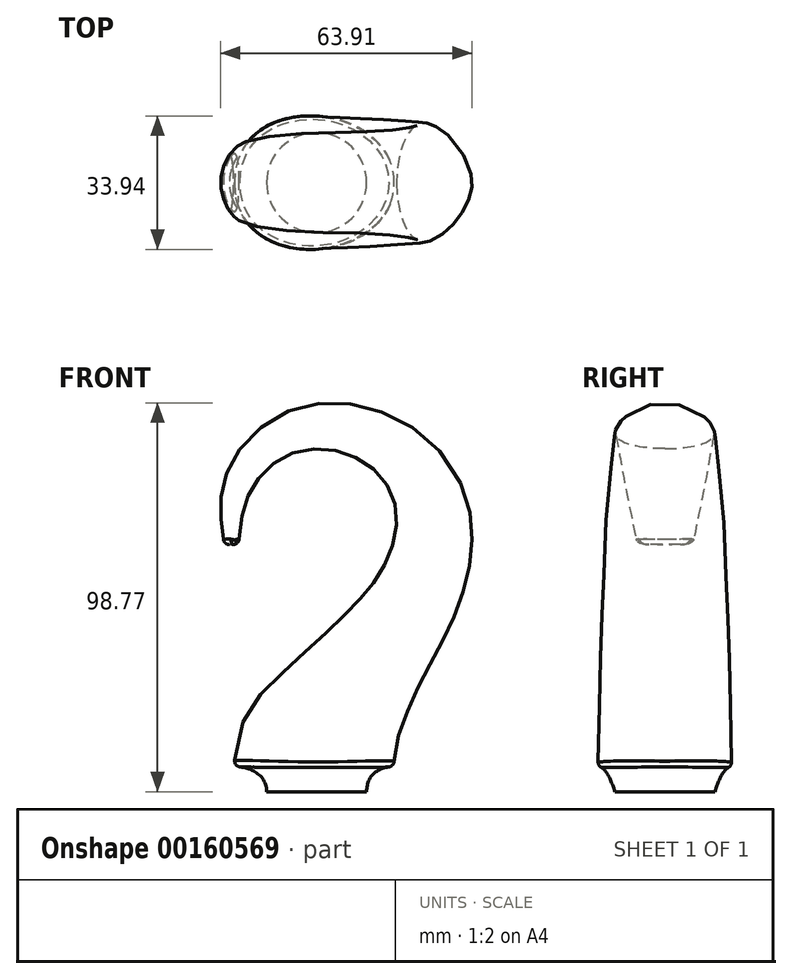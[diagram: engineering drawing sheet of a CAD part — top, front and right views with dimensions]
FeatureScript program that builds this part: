
annotation { "Feature Type Name" : "Feature", "Feature Type Description" : "" }
export const myFeature = defineFeature(function(context is Context, id is Id, definition is map)
    precondition{}
    {
        {
            var Q0;
            Q0=qCreatedBy(makeId("Front.planeOp"),FACE);
            var sketch = newSketch(context, id + "F0", { "sketchPlane" : qUnion([Q0])});
            skFitSpline(sketch, "E0", {"points": [v(-20.88, 0) * mm, v(-8.18, 24.36) * mm, v(6.88, 38.33) * mm, v(16.43, 49.82) * mm, v(20.3, 63.6) * mm, v(14, 76.05) * mm, v(-2.92, 80.53) * mm, v(-15.61, 72.06) * mm, v(-19.79, 56.46) * mm], "startDerivative": vector(0, 244.58) * mm, "endDerivative": vector(-10.5, -156.23) * mm});
            skFitSpline(sketch, "E1", {"points": [v(19.66, 0) * mm, v(22.72, 13.2) * mm, v(28.88, 26.12) * mm, v(36.61, 42.56) * mm, v(38.67, 65.9) * mm, v(23.2, 86.93) * mm, v(-5.21, 91.04) * mm, v(-22.74, 74.84) * mm, v(-23.47, 56.34) * mm], "startDerivative": vector(0, 140.08) * mm, "endDerivative": vector(27.53, -159.04) * mm});
            skLineSegment(sketch, "E2", {"start": v(-20.88, 0) * mm, "end": v(-20.88, 29.57) * mm});
            skLineSegment(sketch, "E3", {"start": v(19.66, 0) * mm, "end": v(19.66, 23.38) * mm});
            skLineSegment(sketch, "E4", {"start": v(-20.88, 0) * mm, "end": v(19.66, 0) * mm});
            skLineSegment(sketch, "E5", {"start": v(-8.18, 24.36) * mm, "end": v(22.72, 13.2) * mm});
            skLineSegment(sketch, "E6", {"start": v(6.88, 38.33) * mm, "end": v(28.88, 26.12) * mm});
            skLineSegment(sketch, "E7", {"start": v(16.43, 49.82) * mm, "end": v(36.61, 42.56) * mm});
            skLineSegment(sketch, "E8", {"start": v(-23.47, 56.34) * mm, "end": v(-19.79, 56.46) * mm});
            skLineSegment(sketch, "E9", {"start": v(20.3, 63.6) * mm, "end": v(38.67, 65.9) * mm});
            skLineSegment(sketch, "E10", {"start": v(14, 76.05) * mm, "end": v(23.2, 86.93) * mm});
            skLineSegment(sketch, "E11", {"start": v(-2.92, 80.53) * mm, "end": v(-5.21, 91.04) * mm});
            skLineSegment(sketch, "E12", {"start": v(-15.61, 72.06) * mm, "end": v(-22.74, 74.84) * mm});
            skLineSegment(sketch, "E13.0", {"start": v(-20.5, -6.35) * mm, "end": v(21.88, -6.35) * mm});
            skLineSegment(sketch, "E14", {"start": v(0, 0) * mm, "end": v(0, -6.35) * mm});
            skFitSpline(sketch, "E15", {"points": [v(-20.88, 0) * mm, v(-12.7, -6.35) * mm], "startDerivative": vector(11.63, 0) * mm, "endDerivative": vector(0, -13.38) * mm});
            skLineSegment(sketch, "E16", {"start": v(-12.7, -6.35) * mm, "end": v(-12.7, 2.57) * mm});
            skFitSpline(sketch, "E17", {"points": [v(12.7, -6.35) * mm, v(19.66, 0) * mm], "startDerivative": vector(0, 13.6) * mm, "endDerivative": vector(10.69, 0) * mm});
            skLineSegment(sketch, "E18", {"start": v(12.7, -6.35) * mm, "end": v(12.7, 2.71) * mm});
            skLineSegment(sketch, "E19", {"start": v(-12.7, -6.35) * mm, "end": v(-12.7, -39.69) * mm});
            skLineSegment(sketch, "E20", {"start": v(12.7, -6.35) * mm, "end": v(12.7, -39.69) * mm});
            skLineSegment(sketch, "E21", {"start": v(-12.7, -39.69) * mm, "end": v(12.7, -39.69) * mm});
            skLineSegment(sketch, "E22", {"start": v(-12.7, -39.69) * mm, "end": v(-12.7, -42.74) * mm});
            skLineSegment(sketch, "E23", {"start": v(-12.7, -42.74) * mm, "end": v(-9.97, -41.04) * mm});
            skLineSegment(sketch, "E24", {"start": v(-9.97, -41.04) * mm, "end": v(-12.7, -39.69) * mm});
            skLineSegment(sketch, "E25", {"start": v(12.7, -36.94) * mm, "end": v(10.62, -40.4) * mm});
            skLineSegment(sketch, "E26", {"start": v(12.7, -39.69) * mm, "end": v(12.7, -41.21) * mm});
            skPoint(sketch, "E26.endSnap0", {"position": v(-12.7, -41.21) * mm});
            skLineSegment(sketch, "E27", {"start": v(10.62, -40.4) * mm, "end": v(12.7, -40.4) * mm});
            skSolve(sketch);
        }
        {
            var Q0;
            Q0 = qSketchRegion(id + "F0", true);
            var Q1;
            Q1=sQuery(id+"F0.wireOp",EDGE,"E4");
            extrude(context, id + "F1", {"entities" : qUnion([Q0]), "bodyType" : ToolBodyType.SURFACE, "surfaceEntities" : qUnion([Q1]), "endBound" : BoundingType.SYMMETRIC, "depth" : 38.1 * mm});
        }
        {
            var Q0;
            Q0 = qSketchRegion(id + "F0", true);
            var Q1;
            Q1=sQuery(id+"F0.wireOp",EDGE,"E5");
            extrude(context, id + "F2", {"entities" : qUnion([Q0]), "bodyType" : ToolBodyType.SURFACE, "surfaceEntities" : qUnion([Q1]), "endBound" : BoundingType.SYMMETRIC, "depth" : 38.1 * mm});
        }
        {
            var Q0;
            Q0=sQuery(id+"F0.wireOp",EDGE,"E6");
            extrude(context, id + "F3", {"bodyType" : ToolBodyType.SURFACE, "surfaceEntities" : qUnion([Q0]), "endBound" : BoundingType.SYMMETRIC, "depth" : 38.1 * mm});
        }
        {
            var Q0;
            {var subQ0=sQuery(id+"F0.wireOp",EDGE,"E6");Q0=makeQuery(id+"F0.imprint","IMPRINT",FACE,{"disambiguationData":[TD([[makeQuery(id+"F0.imprint","IMPRINT",EDGE,{"derivedFrom":subQ0}),1.0]])]});}
            var Q1;
            Q1=sQuery(id+"F0.wireOp",EDGE,"E7");
            extrude(context, id + "F4", {"entities" : qUnion([Q0]), "bodyType" : ToolBodyType.SURFACE, "surfaceEntities" : qUnion([Q1]), "endBound" : BoundingType.SYMMETRIC, "depth" : 38.1 * mm});
        }
        {
            var Q0;
            Q0=sQuery(id+"F0.wireOp",EDGE,"E9");
            extrude(context, id + "F5", {"bodyType" : ToolBodyType.SURFACE, "surfaceEntities" : qUnion([Q0]), "endBound" : BoundingType.SYMMETRIC, "depth" : 38.1 * mm});
        }
        {
            var Q0;
            Q0=sQuery(id+"F0.wireOp",EDGE,"E10");
            extrude(context, id + "F6", {"bodyType" : ToolBodyType.SURFACE, "surfaceEntities" : qUnion([Q0]), "endBound" : BoundingType.SYMMETRIC, "depth" : 31.75 * mm});
        }
        {
            var Q0;
            Q0=sQuery(id+"F0.wireOp",EDGE,"E11");
            extrude(context, id + "F7", {"bodyType" : ToolBodyType.SURFACE, "surfaceEntities" : qUnion([Q0]), "endBound" : BoundingType.SYMMETRIC, "depth" : 31.75 * mm});
        }
        {
            var Q0;
            Q0=sQuery(id+"F0.wireOp",EDGE,"E12");
            extrude(context, id + "F8", {"bodyType" : ToolBodyType.SURFACE, "surfaceEntities" : qUnion([Q0]), "endBound" : BoundingType.SYMMETRIC, "depth" : 28.57 * mm});
        }
        {
            var Q0;
            Q0 = qSketchRegion(id + "F0", true);
            var Q1;
            Q1=sQuery(id+"F0.wireOp",EDGE,"E8");
            extrude(context, id + "F9", {"entities" : qUnion([Q0]), "bodyType" : ToolBodyType.SURFACE, "surfaceEntities" : qUnion([Q1]), "endBound" : BoundingType.SYMMETRIC, "depth" : 25.4 * mm});
        }
        {
            var Q0;
            Q0=makeQuery(id+"F1.opExtrude","SWEPT_FACE",FACE,{"disambiguationData":[OSD([sQuery(id+"F0.wireOp",EDGE,"E4")])]});
            var sketch = newSketch(context, id + "F10", { "sketchPlane" : qUnion([Q0])});
            skFitSpline(sketch, "E28", {"points": [v(-20.88, 0) * mm, v(1.09, -16.87) * mm, v(19.66, 0) * mm], "startDerivative": vector(0, -77.44) * mm, "endDerivative": vector(0, 61.25) * mm});
            skFitSpline(sketch, "E29.MirrorCS", {"points": [v(-20.88, 0) * mm, v(1.09, 16.87) * mm, v(19.66, 0) * mm], "startDerivative": vector(0, 77.44) * mm, "endDerivative": vector(0, -61.25) * mm});
            skSolve(sketch);
        }
        {
            var Q0;
            Q0=makeQuery(id+"F2.opExtrude","SWEPT_FACE",FACE,{"disambiguationData":[OSD([sQuery(id+"F0.wireOp",EDGE,"E5")])]});
            var sketch = newSketch(context, id + "F11", { "sketchPlane" : qUnion([Q0])});
            skFitSpline(sketch, "E30", {"points": [v(-15.97, 0) * mm, v(-3.43, -16.52) * mm, v(16.88, 0) * mm], "startDerivative": vector(0, -47.06) * mm, "endDerivative": vector(0, 47.26) * mm});
            skFitSpline(sketch, "E31.MirrorCS", {"points": [v(-15.97, 0) * mm, v(-3.43, 16.52) * mm, v(16.88, 0) * mm], "startDerivative": vector(0, 47.06) * mm, "endDerivative": vector(0, -47.26) * mm});
            skSolve(sketch);
        }
        {
            var Q0;
            Q0=makeQuery(id+"F3.opExtrude","SWEPT_FACE",FACE,{"disambiguationData":[OSD([sQuery(id+"F0.wireOp",EDGE,"E6")])]});
            var sketch = newSketch(context, id + "F12", { "sketchPlane" : qUnion([Q0])});
            skFitSpline(sketch, "E32", {"points": [v(-12.59, 0) * mm, v(-4.6, -16.15) * mm, v(12.57, 0) * mm], "startDerivative": vector(0, -57.35) * mm, "endDerivative": vector(0, 43.44) * mm});
            skFitSpline(sketch, "E33.MirrorCS", {"points": [v(-12.59, 0) * mm, v(-4.6, 16.15) * mm, v(12.57, 0) * mm], "startDerivative": vector(0, 57.35) * mm, "endDerivative": vector(0, -43.44) * mm});
            skSolve(sketch);
        }
        {
            var Q0;
            Q0=makeQuery(id+"F4.opExtrude","SWEPT_FACE",FACE,{"disambiguationData":[OSD([sQuery(id+"F0.wireOp",EDGE,"E7")])]});
            var sketch = newSketch(context, id + "F13", { "sketchPlane" : qUnion([Q0])});
            skFitSpline(sketch, "E34", {"points": [v(-1.38, 0) * mm, v(6.22, -15.51) * mm, v(20.07, 0) * mm], "startDerivative": vector(0, -37.32) * mm, "endDerivative": vector(0, 31.05) * mm});
            skFitSpline(sketch, "E35.MirrorCS", {"points": [v(-1.38, 0) * mm, v(6.22, 15.51) * mm, v(20.07, 0) * mm], "startDerivative": vector(0, 37.32) * mm, "endDerivative": vector(0, -31.05) * mm});
            skSolve(sketch);
        }
        {
            var Q0;
            Q0=makeQuery(id+"F5.opExtrude","SWEPT_FACE",FACE,{"disambiguationData":[OSD([sQuery(id+"F0.wireOp",EDGE,"E9")])]});
            var sketch = newSketch(context, id + "F14", { "sketchPlane" : qUnion([Q0])});
            skFitSpline(sketch, "E36", {"points": [v(28.03, 0) * mm, v(34.37, -14.78) * mm, v(46.54, 0) * mm], "startDerivative": vector(0, -41.23) * mm, "endDerivative": vector(0, 41.24) * mm});
            skFitSpline(sketch, "E37.MirrorCS", {"points": [v(28.03, 0) * mm, v(34.37, 14.78) * mm, v(46.54, 0) * mm], "startDerivative": vector(0, 41.23) * mm, "endDerivative": vector(0, -41.24) * mm});
            skSolve(sketch);
        }
        {
            var Q0;
            Q0=makeQuery(id+"F6.opExtrude","SWEPT_FACE",FACE,{"disambiguationData":[OSD([sQuery(id+"F0.wireOp",EDGE,"E10")])]});
            var sketch = newSketch(context, id + "F15", { "sketchPlane" : qUnion([Q0])});
            skFitSpline(sketch, "E38", {"points": [v(0, 67.14) * mm, v(13.2, 71.95) * mm, v(0, 81.38) * mm], "startDerivative": vector(47.39, 0) * mm, "endDerivative": vector(-38.47, 0) * mm});
            skFitSpline(sketch, "E39.MirrorCS", {"points": [v(0, 67.14) * mm, v(-13.2, 71.95) * mm, v(0, 81.38) * mm], "startDerivative": vector(-47.39, 0) * mm, "endDerivative": vector(38.47, 0) * mm});
            skSolve(sketch);
        }
        {
            var Q0;
            Q0=makeQuery(id+"F7.opExtrude","SWEPT_FACE",FACE,{"disambiguationData":[OSD([sQuery(id+"F0.wireOp",EDGE,"E11")])]});
            var sketch = newSketch(context, id + "F16", { "sketchPlane" : qUnion([Q0])});
            skFitSpline(sketch, "E40", {"points": [v(0, 79.3) * mm, v(-12.36, 82.69) * mm, v(0, 90.06) * mm], "startDerivative": vector(-27.64, 0) * mm, "endDerivative": vector(39.98, 0) * mm});
            skFitSpline(sketch, "E41.MirrorCS", {"points": [v(0, 79.3) * mm, v(12.36, 82.69) * mm, v(0, 90.06) * mm], "startDerivative": vector(27.64, 0) * mm, "endDerivative": vector(-39.98, 0) * mm});
            skSolve(sketch);
        }
        {
            var Q0;
            Q0=makeQuery(id+"F8.opExtrude","SWEPT_FACE",FACE,{"disambiguationData":[OSD([sQuery(id+"F0.wireOp",EDGE,"E12")])]});
            var sketch = newSketch(context, id + "F17", { "sketchPlane" : qUnion([Q0])});
            skFitSpline(sketch, "E42", {"points": [v(-40.71, 0) * mm, v(-42.92, -10.35) * mm, v(-48.37, 0) * mm], "startDerivative": vector(0, -20.7) * mm, "endDerivative": vector(0, 25.7) * mm});
            skFitSpline(sketch, "E43.MirrorCS", {"points": [v(-40.71, 0) * mm, v(-42.92, 10.35) * mm, v(-48.37, 0) * mm], "startDerivative": vector(0, 20.7) * mm, "endDerivative": vector(0, -25.7) * mm});
            skSolve(sketch);
        }
        {
            var Q0;
            Q0=makeQuery(id+"F9.opExtrude","SWEPT_FACE",FACE,{"disambiguationData":[OSD([sQuery(id+"F0.wireOp",EDGE,"E8")])]});
            var sketch = newSketch(context, id + "F18", { "sketchPlane" : qUnion([Q0])});
            skFitSpline(sketch, "E44", {"points": [v(-17.94, 0) * mm, v(-18.9, 7.05) * mm, v(-21.62, 0) * mm], "startDerivative": vector(0, 12.16) * mm, "endDerivative": vector(0, -22.35) * mm});
            skFitSpline(sketch, "E45.MirrorCS", {"points": [v(-17.94, 0) * mm, v(-18.9, -7.05) * mm, v(-21.62, 0) * mm], "startDerivative": vector(0, -12.16) * mm, "endDerivative": vector(0, 22.35) * mm});
            skSolve(sketch);
        }
        {
            var Q0;
            Q0 = qSketchRegion(id + "F0", true);
            var Q1;
            Q1=sQuery(id+"F0.wireOp",EDGE,"E13.0");
            extrude(context, id + "F19", {"entities" : qUnion([Q0]), "bodyType" : ToolBodyType.SURFACE, "surfaceEntities" : qUnion([Q1]), "endBound" : BoundingType.SYMMETRIC, "depth" : 25.4 * mm});
        }
        {
            var Q0;
            Q0=makeQuery(id+"F19.opExtrude","SWEPT_FACE",FACE,{"disambiguationData":[OSD([sQuery(id+"F0.wireOp",EDGE,"E13.0")])]});
            var sketch = newSketch(context, id + "F20", { "sketchPlane" : qUnion([Q0])});
            skCircle(sketch, "E46", {"center": v(0, 0) * mm, "radius": 12.7 * mm});
            skSolve(sketch);
        }
        {
            var Q0;
            Q0=makeQuery(id+"F10.imprint","IMPRINT",FACE,{"disambiguationData":[TD([[makeQuery(id+"F10.imprint","IMPRINT",EDGE,{"derivedFrom":sQuery(id+"F10.wireOp",EDGE,"E28")}),1.0]])]});
            var Q1;
            {var subQ0=sQuery(id+"F20.wireOp",EDGE,"E46");var subQ1=sQuery(id+"F0.wireOp",EDGE,"E13.0");var subQ2=makeQuery(id+"F20.imprint","INTERSECT",VERTEX,{"derivedFrom":[makeQuery(id+"F19.opExtrude","CAP_EDGE",EDGE,{"disambiguationData":[OSD([subQ1])],"isStart":true}),subQ0]});Q1=makeQuery(id+"F20.imprint","IMPRINT",FACE,{"disambiguationData":[TD([[makeQuery(id+"F20.imprint","IMPRINT",EDGE,{"disambiguationData":[TD([[subQ2,1.0]])],"derivedFrom":subQ0}),1.0]])]});}
            var Q2;
            Q2=sQuery(id+"F0.wireOp",EDGE,"E15");
            var Q3;
            Q3=sQuery(id+"F0.wireOp",EDGE,"E17");
            loft(context, id + "F21", {"addGuides" : true, "sheetProfilesArray" : [{ "sheetProfileEntities" : qUnion([Q0]) }, { "sheetProfileEntities" : qUnion([Q1]) }], "guidesArray" : [{ "guideEntities" : qUnion([Q2]), "guideDerivativeType" : LoftGuideDerivativeType.DEFAULT, "guideDerivativeMagnitude" : 1 }, { "guideEntities" : qUnion([Q3]), "guideDerivativeType" : LoftGuideDerivativeType.DEFAULT, "guideDerivativeMagnitude" : 1 }]});
        }
        {
            var Q0;
            Q0=makeQuery(id+"F10.imprint","IMPRINT",FACE,{"disambiguationData":[TD([[makeQuery(id+"F10.imprint","IMPRINT",EDGE,{"derivedFrom":sQuery(id+"F10.wireOp",EDGE,"E28")}),1.0]])]});
            var Q1;
            Q1=makeQuery(id+"F11.imprint","IMPRINT",FACE,{"disambiguationData":[TD([[makeQuery(id+"F11.imprint","IMPRINT",EDGE,{"derivedFrom":sQuery(id+"F11.wireOp",EDGE,"E30")}),1.0]])]});
            var Q2;
            Q2=makeQuery(id+"F12.imprint","IMPRINT",FACE,{"disambiguationData":[TD([[makeQuery(id+"F12.imprint","IMPRINT",EDGE,{"derivedFrom":sQuery(id+"F12.wireOp",EDGE,"E32")}),1.0]])]});
            var Q3;
            Q3=makeQuery(id+"F13.imprint","IMPRINT",FACE,{"disambiguationData":[TD([[makeQuery(id+"F13.imprint","IMPRINT",EDGE,{"derivedFrom":sQuery(id+"F13.wireOp",EDGE,"E34")}),1.0]])]});
            var Q4;
            {var subQ1=sQuery(id+"F14.wireOp",EDGE,"E36");var subQ3=makeQuery(id+"F5.opExtrude","SWEPT_EDGE",EDGE,{"disambiguationData":[OSD([sQuery(id+"F0.wireOp",VERTEX,"E9.start")])]});var subQ4=makeQuery(id+"F14.imprint","INTERSECT",VERTEX,{"derivedFrom":[subQ3,subQ1]});Q4=makeQuery(id+"F14.imprint","IMPRINT",FACE,{"disambiguationData":[TD([[makeQuery(id+"F14.imprint","IMPRINT",EDGE,{"disambiguationData":[TD([[subQ4,-1.0]])],"derivedFrom":subQ1}),1.0]])]});}
            var Q5;
            Q5=makeQuery(id+"F15.imprint","IMPRINT",FACE,{"disambiguationData":[TD([[makeQuery(id+"F15.imprint","IMPRINT",EDGE,{"derivedFrom":sQuery(id+"F15.wireOp",EDGE,"E38")}),1.0]])]});
            var Q6;
            {var subQ1=sQuery(id+"F16.wireOp",EDGE,"E40");var subQ3=makeQuery(id+"F7.opExtrude","SWEPT_EDGE",EDGE,{"disambiguationData":[OSD([sQuery(id+"F0.wireOp",VERTEX,"E11.start")])]});var subQ4=makeQuery(id+"F16.imprint","INTERSECT",VERTEX,{"derivedFrom":[subQ3,subQ1]});Q6=makeQuery(id+"F16.imprint","IMPRINT",FACE,{"disambiguationData":[TD([[makeQuery(id+"F16.imprint","IMPRINT",EDGE,{"disambiguationData":[TD([[subQ4,-1.0]])],"derivedFrom":subQ1}),-1.0]])]});}
            var Q7;
            Q7=makeQuery(id+"F17.imprint","IMPRINT",FACE,{"disambiguationData":[TD([[makeQuery(id+"F17.imprint","IMPRINT",EDGE,{"derivedFrom":sQuery(id+"F17.wireOp",EDGE,"E42")}),-1.0]])]});
            var Q8;
            {var subQ1=sQuery(id+"F18.wireOp",EDGE,"E44");var subQ3=makeQuery(id+"F9.opExtrude","SWEPT_EDGE",EDGE,{"disambiguationData":[OSD([sQuery(id+"F0.wireOp",VERTEX,"E8.end")])]});var subQ4=makeQuery(id+"F18.imprint","INTERSECT",VERTEX,{"derivedFrom":[subQ3,subQ1]});Q8=makeQuery(id+"F18.imprint","IMPRINT",FACE,{"disambiguationData":[TD([[makeQuery(id+"F18.imprint","IMPRINT",EDGE,{"disambiguationData":[TD([[subQ4,-1.0]])],"derivedFrom":subQ1}),1.0]])]});}
            var Q9;
            Q9=sQuery(id+"F0.wireOp",EDGE,"E0");
            var Q10;
            Q10=sQuery(id+"F0.wireOp",EDGE,"E1");
            loft(context, id + "F22", {"addGuides" : true, "sheetProfilesArray" : [{ "sheetProfileEntities" : qUnion([Q0]) }, { "sheetProfileEntities" : qUnion([Q1]) }, { "sheetProfileEntities" : qUnion([Q2]) }, { "sheetProfileEntities" : qUnion([Q3]) }, { "sheetProfileEntities" : qUnion([Q4]) }, { "sheetProfileEntities" : qUnion([Q5]) }, { "sheetProfileEntities" : qUnion([Q6]) }, { "sheetProfileEntities" : qUnion([Q7]) }, { "sheetProfileEntities" : qUnion([Q8]) }], "guidesArray" : [{ "guideEntities" : qUnion([Q9]), "guideDerivativeType" : LoftGuideDerivativeType.DEFAULT, "guideDerivativeMagnitude" : 1 }, { "guideEntities" : qUnion([Q10]), "guideDerivativeType" : LoftGuideDerivativeType.DEFAULT, "guideDerivativeMagnitude" : 1 }]});
        }
        {
            var Q0;
            Q0=makeQuery(id+"F22.opLoft","SWEPT_BODY",BODY,{"disambiguationData":[OSD([sQuery(id+"F0.wireOp",EDGE,"E0"),sQuery(id+"F0.wireOp",EDGE,"E1"),makeQuery(id+"F10.imprint","IMPRINT",FACE,{"disambiguationData":[TD([[makeQuery(id+"F10.imprint","IMPRINT",EDGE,{"derivedFrom":sQuery(id+"F10.wireOp",EDGE,"E28")}),1.0]])]}),sQuery(id+"F11.wireOp",EDGE,"E31.MirrorCS"),sQuery(id+"F12.wireOp",EDGE,"E33.MirrorCS"),sQuery(id+"F13.wireOp",EDGE,"E35.MirrorCS"),sQuery(id+"F14.wireOp",EDGE,"E37.MirrorCS"),sQuery(id+"F15.wireOp",EDGE,"E39.MirrorCS"),sQuery(id+"F16.wireOp",EDGE,"E40"),sQuery(id+"F17.wireOp",EDGE,"E42"),makeQuery(id+"F18.imprint","IMPRINT",FACE,{"disambiguationData":[TD([[makeQuery(id+"F18.imprint","IMPRINT",EDGE,{"derivedFrom":sQuery(id+"F18.wireOp",EDGE,"E44")}),1.0]])]})])]});
            var Q1;
            {var subQ0=sQuery(id+"F20.wireOp",EDGE,"E46");var subQ1=sQuery(id+"F0.wireOp",EDGE,"E13.0");var subQ2=makeQuery(id+"F20.imprint","INTERSECT",VERTEX,{"derivedFrom":[makeQuery(id+"F19.opExtrude","CAP_EDGE",EDGE,{"disambiguationData":[OSD([subQ1])],"isStart":true}),subQ0]});Q1=makeQuery(id+"F21.opLoft","SWEPT_BODY",BODY,{"disambiguationData":[OSD([sQuery(id+"F0.wireOp",EDGE,"E15"),sQuery(id+"F0.wireOp",EDGE,"E17"),makeQuery(id+"F10.imprint","IMPRINT",FACE,{"disambiguationData":[TD([[makeQuery(id+"F10.imprint","IMPRINT",EDGE,{"derivedFrom":sQuery(id+"F10.wireOp",EDGE,"E28")}),1.0]])]}),makeQuery(id+"F20.imprint","IMPRINT",FACE,{"disambiguationData":[TD([[makeQuery(id+"F20.imprint","IMPRINT",EDGE,{"disambiguationData":[TD([[subQ2,1.0]])],"derivedFrom":subQ0}),1.0]])]})])]});}
            booleanBodies(context, id + "F23", {"operationType" : BooleanOperationType.UNION, "tools" : qUnion([Q0, Q1])});
        }
        {
            var Q0;
            {var subQ0=sQuery(id+"F10.wireOp",EDGE,"E29.MirrorCS");Q0=makeQuery(id+"F23.opBoolean","MERGE",EDGE,{"derivedFrom":[makeQuery(id+"F21.opLoft","MID_CAP_EDGE",EDGE,{"disambiguationData":[OSD([sQuery(id+"F0.wireOp",EDGE,"E15"),sQuery(id+"F0.wireOp",EDGE,"E17"),subQ0])],"capPos":0.0}),makeQuery(id+"F22.opLoft","MID_CAP_EDGE",EDGE,{"disambiguationData":[OSD([sQuery(id+"F0.wireOp",EDGE,"E0"),sQuery(id+"F0.wireOp",EDGE,"E1"),subQ0])],"capPos":0.0})]});}
            var Q1;
            {var subQ0=sQuery(id+"F10.wireOp",EDGE,"E29.MirrorCS");Q1=makeQuery(id+"F23.opBoolean","MERGE",EDGE,{"derivedFrom":[makeQuery(id+"F21.opLoft","MID_CAP_EDGE",EDGE,{"disambiguationData":[OSD([sQuery(id+"F0.wireOp",EDGE,"E17"),subQ0])],"capPos":0.0}),makeQuery(id+"F22.opLoft","MID_CAP_EDGE",EDGE,{"disambiguationData":[OSD([sQuery(id+"F0.wireOp",EDGE,"E0"),sQuery(id+"F0.wireOp",EDGE,"E1"),subQ0])],"capPos":0.0})]});}
            var Q2;
            {var subQ0=sQuery(id+"F10.wireOp",EDGE,"E28");Q2=makeQuery(id+"F23.opBoolean","MERGE",EDGE,{"derivedFrom":[makeQuery(id+"F21.opLoft","MID_CAP_EDGE",EDGE,{"disambiguationData":[OSD([sQuery(id+"F0.wireOp",EDGE,"E15"),sQuery(id+"F0.wireOp",EDGE,"E17"),subQ0])],"capPos":0.0}),makeQuery(id+"F22.opLoft","MID_CAP_EDGE",EDGE,{"disambiguationData":[OSD([sQuery(id+"F0.wireOp",EDGE,"E0"),sQuery(id+"F0.wireOp",EDGE,"E1"),subQ0])],"capPos":0.0})]});}
            var Q3;
            {var subQ0=sQuery(id+"F10.wireOp",EDGE,"E28");Q3=makeQuery(id+"F23.opBoolean","MERGE",EDGE,{"derivedFrom":[makeQuery(id+"F21.opLoft","MID_CAP_EDGE",EDGE,{"disambiguationData":[OSD([sQuery(id+"F0.wireOp",EDGE,"E15"),subQ0])],"capPos":0.0}),makeQuery(id+"F22.opLoft","MID_CAP_EDGE",EDGE,{"disambiguationData":[OSD([sQuery(id+"F0.wireOp",EDGE,"E0"),sQuery(id+"F0.wireOp",EDGE,"E1"),subQ0])],"capPos":0.0})]});}
            fillet(context, id + "F24", {"entities" : qUnion([Q0, Q1, Q2, Q3]), "radius" : 1.59 * mm, "tangentPropagation" : true, "allowEdgeOverflow" : false});
        }
        {
            var Q0;
            Q0=makeQuery(id+"F22.opLoft","MID_CAP_EDGE",EDGE,{"disambiguationData":[OSD([sQuery(id+"F0.wireOp",EDGE,"E0"),sQuery(id+"F0.wireOp",EDGE,"E1"),sQuery(id+"F18.wireOp",EDGE,"E44")])],"capPos":8.0});
            var Q1;
            Q1=makeQuery(id+"F22.opLoft","MID_CAP_EDGE",EDGE,{"disambiguationData":[OSD([sQuery(id+"F0.wireOp",EDGE,"E0"),sQuery(id+"F0.wireOp",EDGE,"E1"),sQuery(id+"F18.wireOp",EDGE,"E45.MirrorCS")])],"capPos":8.0});
            fillet(context, id + "F25", {"entities" : qUnion([Q0, Q1]), "radius" : 1.59 * mm, "tangentPropagation" : true, "allowEdgeOverflow" : false});
        }
    });
